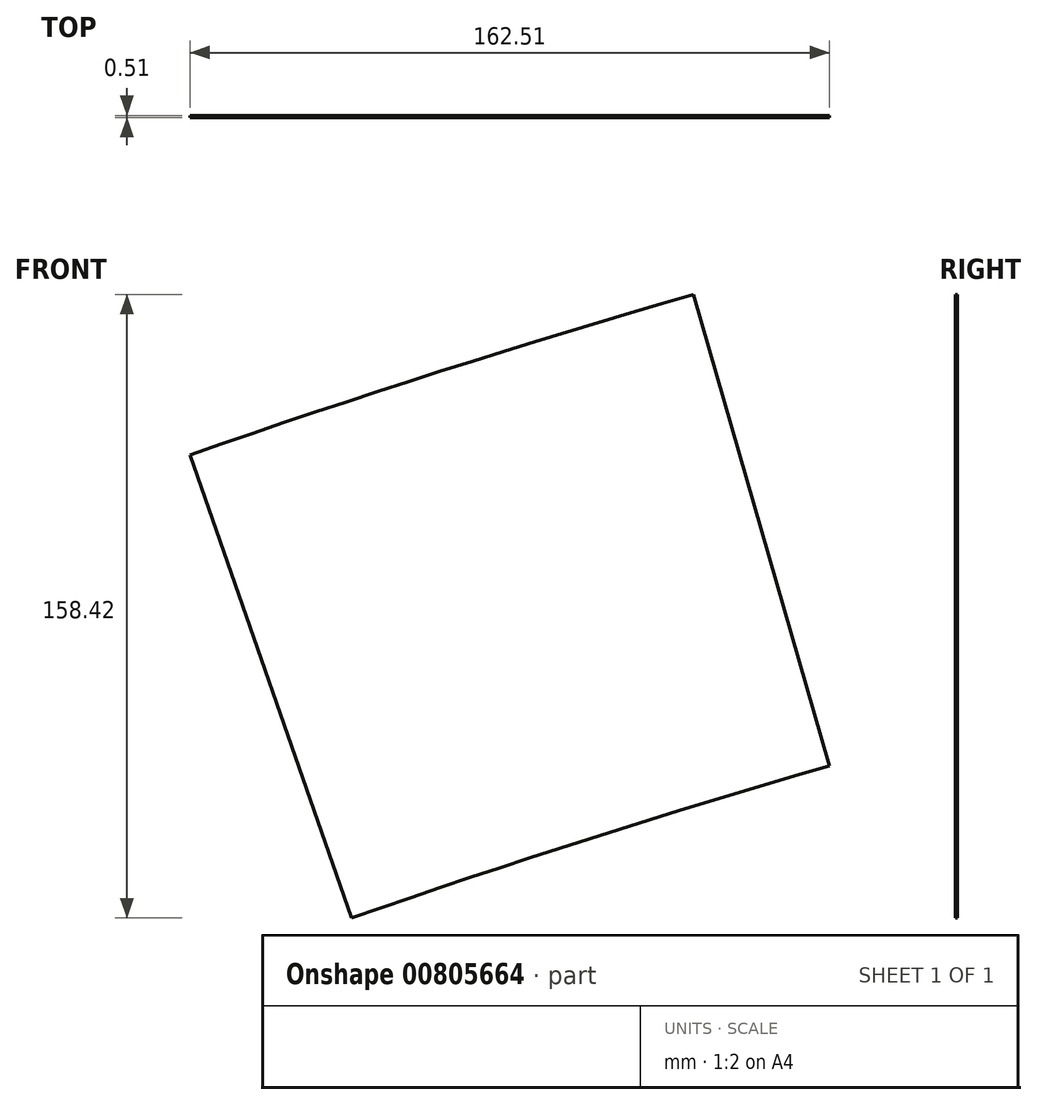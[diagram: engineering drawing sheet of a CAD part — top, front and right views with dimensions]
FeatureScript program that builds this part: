
annotation { "Feature Type Name" : "Feature", "Feature Type Description" : "" }
export const myFeature = defineFeature(function(context is Context, id is Id, definition is map)
    precondition{}
    {
        {
            var Q0;
            Q0=qCreatedBy(makeId("Front.planeOp"),FACE);
            var sketch = newSketch(context, id + "F0", { "sketchPlane" : qUnion([Q0])});
            skArc(sketch, "E0", {"start": v(-642.27, 2228.15) * mm, "mid": v(-703.27, 2209.65) * mm, "end": v(-763.73, 2189.49) * mm});
            skArc(sketch, "E1", {"start": v(-676.79, 2347.9) * mm, "mid": v(-741.07, 2328.42) * mm, "end": v(-804.78, 2307.17) * mm});
            skLineSegment(sketch, "E2", {"start": v(-642.27, 2228.15) * mm, "end": v(-676.79, 2347.9) * mm});
            skLineSegment(sketch, "E3", {"start": v(-763.73, 2189.49) * mm, "end": v(-804.78, 2307.17) * mm});
            skSolve(sketch);
        }
        {
            var Q0;
            Q0=makeQuery(id+"F0.imprint","IMPRINT",FACE,{"disambiguationData":[TD([[makeQuery(id+"F0.imprint","IMPRINT",EDGE,{"derivedFrom":sQuery(id+"F0.wireOp",EDGE,"E0")}),-1.0]])]});
            extrude(context, id + "F1", {"entities" : qUnion([Q0]), "depth" : 0.51 * mm, "offsetDistance" : 25.4 * mm});
        }
    });
